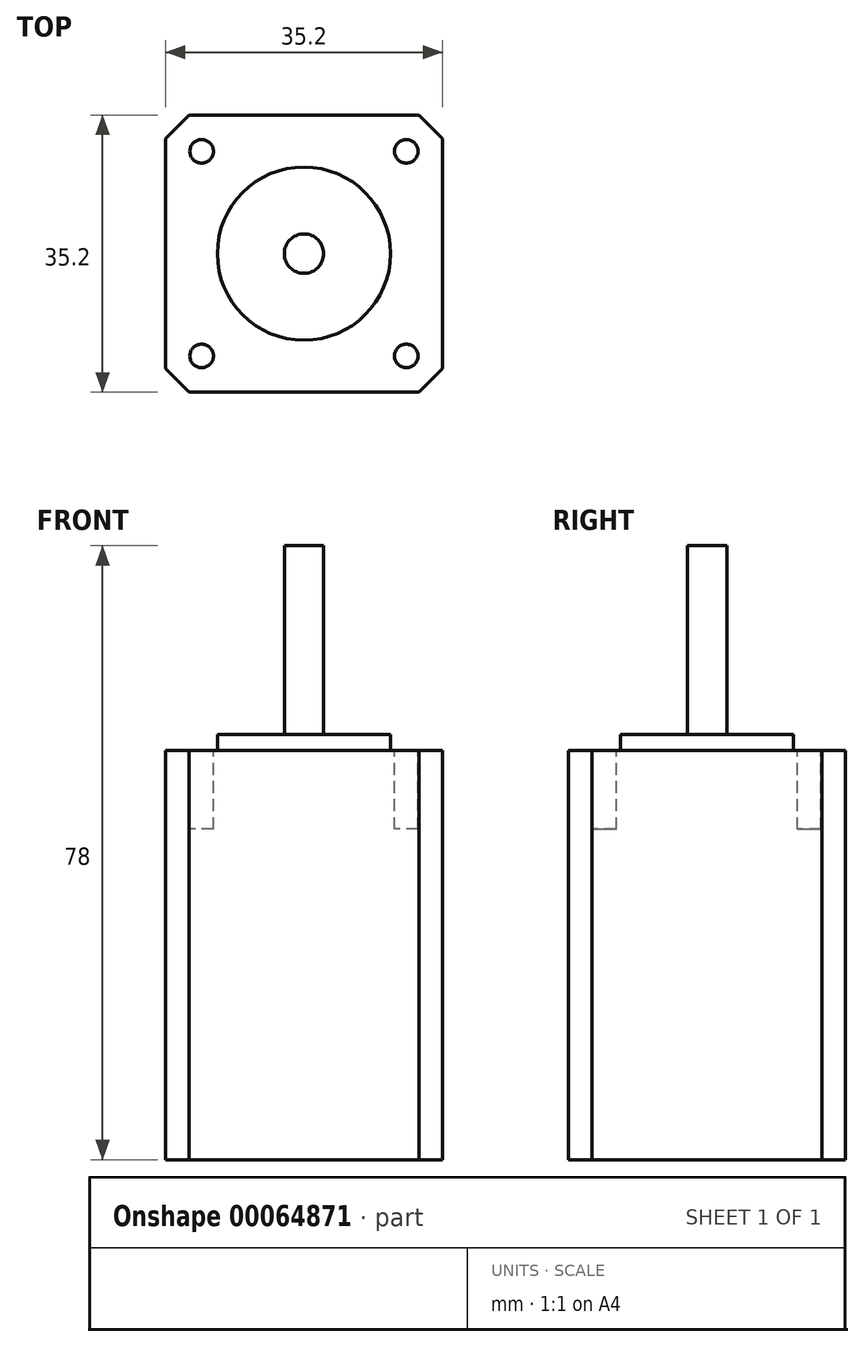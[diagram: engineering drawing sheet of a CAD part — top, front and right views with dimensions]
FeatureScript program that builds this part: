
annotation { "Feature Type Name" : "Feature", "Feature Type Description" : "" }
export const myFeature = defineFeature(function(context is Context, id is Id, definition is map)
    precondition{}
    {
        {
            var Q0;
            Q0=qCreatedBy(makeId("Top.planeOp"),FACE);
            var sketch = newSketch(context, id + "F0", { "sketchPlane" : qUnion([Q0])});
            skLineSegment(sketch, "E0.bottom", {"start": v(0, 0) * mm, "end": v(35.2, 0) * mm});
            skLineSegment(sketch, "E0.top", {"start": v(0, 35.2) * mm, "end": v(35.2, 35.2) * mm});
            skLineSegment(sketch, "E0.left", {"start": v(0, 0) * mm, "end": v(0, 35.2) * mm});
            skLineSegment(sketch, "E0.right", {"start": v(35.2, 0) * mm, "end": v(35.2, 35.2) * mm});
            skSolve(sketch);
        }
        {
            var Q0;
            Q0=qSketchRegion(id+"F0",true);
            extrude(context, id + "F1", {"entities" : qUnion([Q0]), "depth" : 52 * mm});
        }
        {
            var Q0;
            Q0=makeQuery(id+"F1.opExtrude","SWEPT_EDGE",EDGE,{"disambiguationData":[OSD([sQuery(id+"F0.wireOp",EDGE,"E0.bottom"),sQuery(id+"F0.wireOp",EDGE,"E0.left")])]});
            var Q1;
            Q1=makeQuery(id+"F1.opExtrude","SWEPT_EDGE",EDGE,{"disambiguationData":[OSD([sQuery(id+"F0.wireOp",EDGE,"E0.top"),sQuery(id+"F0.wireOp",EDGE,"E0.left")])]});
            var Q2;
            Q2=makeQuery(id+"F1.opExtrude","SWEPT_EDGE",EDGE,{"disambiguationData":[OSD([sQuery(id+"F0.wireOp",EDGE,"E0.bottom"),sQuery(id+"F0.wireOp",EDGE,"E0.right")])]});
            var Q3;
            Q3=makeQuery(id+"F1.opExtrude","SWEPT_EDGE",EDGE,{"disambiguationData":[OSD([sQuery(id+"F0.wireOp",EDGE,"E0.top"),sQuery(id+"F0.wireOp",EDGE,"E0.right")])]});
            chamfer(context, id + "F2", {"entities" : qUnion([Q0, Q1, Q2, Q3]), "width" : 3 * mm, "tangentPropagation" : true});
        }
        {
            var Q0;
            Q0=makeQuery(id+"F1.opExtrude","CAP_FACE",FACE,{"disambiguationData":[OSD([sQuery(id+"F0.wireOp",EDGE,"E0.bottom"),sQuery(id+"F0.wireOp",EDGE,"E0.top"),sQuery(id+"F0.wireOp",EDGE,"E0.left"),sQuery(id+"F0.wireOp",EDGE,"E0.right")])],"isStart":false});
            var sketch = newSketch(context, id + "F3", { "sketchPlane" : qUnion([Q0])});
            skCircle(sketch, "E1", {"center": v(17.6, 17.6) * mm, "radius": 11 * mm});
            skLineSegment(sketch, "E2", {"start": v(17.6, 35.2) * mm, "end": v(17.6, 0) * mm, "construction": true});
            skSolve(sketch);
        }
        {
            var Q0;
            Q0=qSketchRegion(id+"F3",true);
            extrude(context, id + "F4", {"entities" : qUnion([Q0]), "operationType" : NewBodyOperationType.ADD, "depth" : 2 * mm});
        }
        {
            var Q0;
            Q0=makeQuery(id+"F4.opExtrude","CAP_FACE",FACE,{"disambiguationData":[OSD([sQuery(id+"F3.wireOp",EDGE,"E1")])],"isStart":false});
            var sketch = newSketch(context, id + "F5", { "sketchPlane" : qUnion([Q0])});
            skCircle(sketch, "E3", {"center": v(17.6, 17.6) * mm, "radius": 2.5 * mm});
            skSolve(sketch);
        }
        {
            var Q0;
            Q0=qSketchRegion(id+"F5",true);
            var Q1;
            Q1 = qSketchRegion(id + "F7", true);
            extrude(context, id + "F6", {"entities" : qUnion([Q0, Q1]), "operationType" : NewBodyOperationType.ADD, "depth" : 24 * mm});
        }
        {
            var Q0;
            Q0=makeQuery(id+"F1.opExtrude","CAP_FACE",FACE,{"disambiguationData":[OSD([sQuery(id+"F0.wireOp",EDGE,"E0.bottom"),sQuery(id+"F0.wireOp",EDGE,"E0.top"),sQuery(id+"F0.wireOp",EDGE,"E0.left"),sQuery(id+"F0.wireOp",EDGE,"E0.right")])],"isStart":false});
            var sketch = newSketch(context, id + "F7", { "sketchPlane" : qUnion([Q0])});
            skCircle(sketch, "E4", {"center": v(4.6, 30.6) * mm, "radius": 1.5 * mm});
            skCircle(sketch, "E5", {"center": v(4.6, 4.6) * mm, "radius": 1.5 * mm});
            skCircle(sketch, "E6", {"center": v(30.6, 30.6) * mm, "radius": 1.5 * mm});
            skCircle(sketch, "E7", {"center": v(30.6, 4.6) * mm, "radius": 1.5 * mm});
            skLineSegment(sketch, "E8", {"start": v(0, 17.6) * mm, "end": v(35.2, 17.6) * mm, "construction": true});
            skLineSegment(sketch, "E9", {"start": v(17.6, 17.6) * mm, "end": v(17.6, 35.2) * mm, "construction": true});
            skSolve(sketch);
        }
        {
            var Q0;
            Q0=qSketchRegion(id+"F7",true);
            extrude(context, id + "F8", {"entities" : qUnion([Q0]), "operationType" : NewBodyOperationType.REMOVE, "oppositeDirection" : true, "depth" : 10 * mm});
        }
    });
